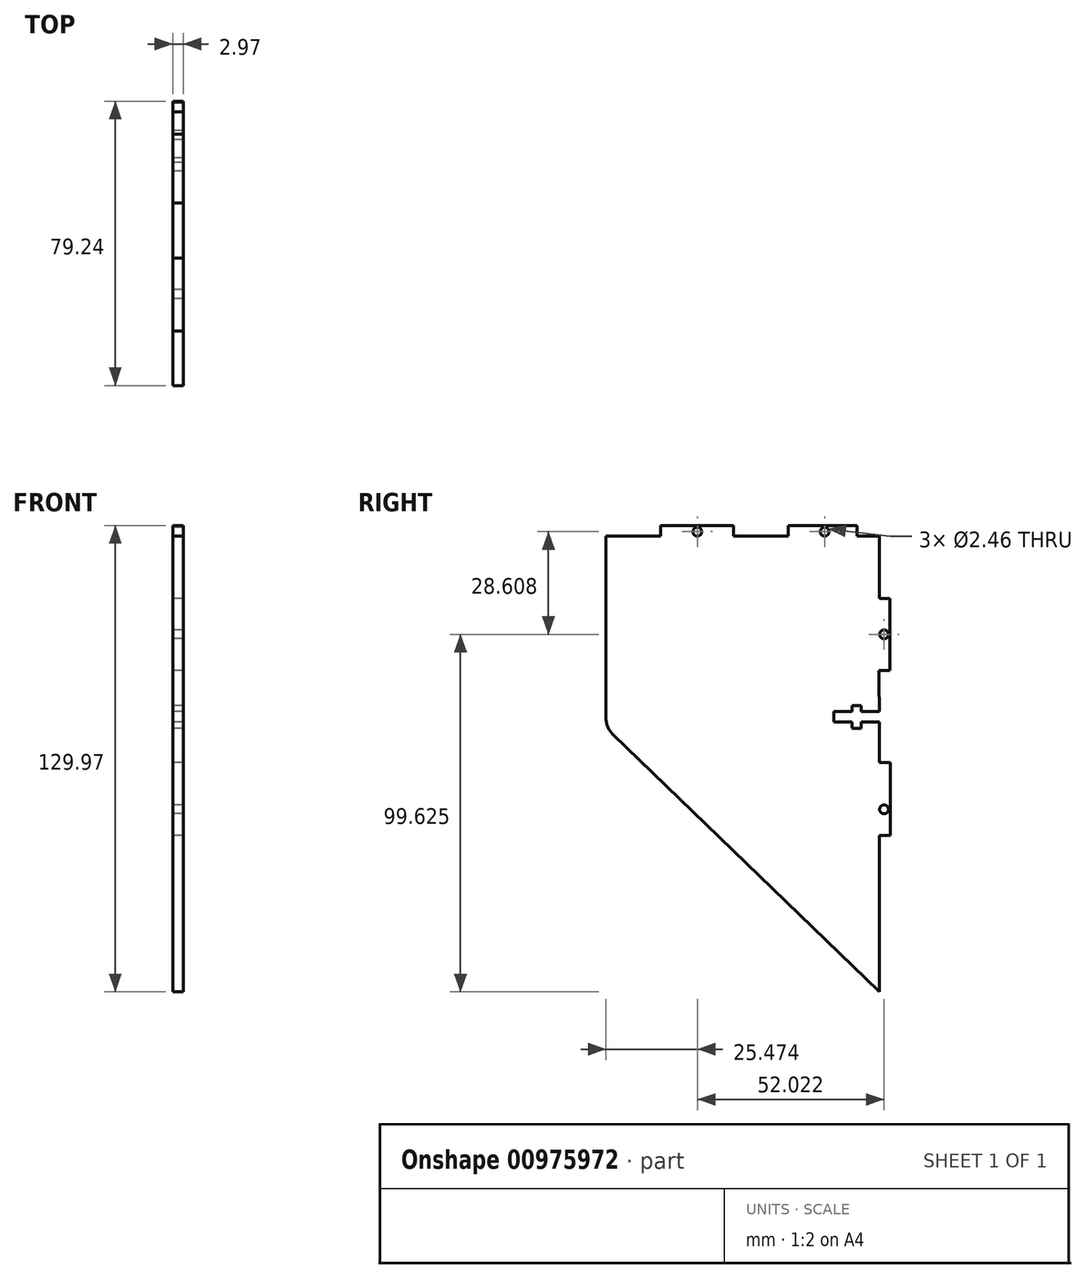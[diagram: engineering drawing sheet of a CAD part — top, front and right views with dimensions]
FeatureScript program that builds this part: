
annotation { "Feature Type Name" : "Feature", "Feature Type Description" : "" }
export const myFeature = defineFeature(function(context is Context, id is Id, definition is map)
    precondition{}
    {
        {
            var Q0;
            Q0=qCreatedBy(makeId("Right.planeOp"),FACE);
            var sketch = newSketch(context, id + "F0", { "sketchPlane" : qUnion([Q0])});
            skLineSegment(sketch, "E0", {"start": v(-31.9, 69.4) * mm, "end": v(-36.98, 69.4) * mm});
            skLineSegment(sketch, "E1", {"start": v(-57.29, 69.4) * mm, "end": v(-72.6, 69.4) * mm});
            skLineSegment(sketch, "E2", {"start": v(-31.9, -16.97) * mm, "end": v(-31.9, -57.6) * mm});
            skLineSegment(sketch, "E3", {"start": v(-92.92, 69.4) * mm, "end": v(-92.92, 72.36) * mm});
            skLineSegment(sketch, "E4", {"start": v(-72.6, 69.4) * mm, "end": v(-72.6, 72.36) * mm});
            skLineSegment(sketch, "E5", {"start": v(-92.92, 72.36) * mm, "end": v(-72.6, 72.36) * mm});
            skLineSegment(sketch, "E6", {"start": v(-108.16, 69.4) * mm, "end": v(-92.92, 69.4) * mm});
            skLineSegment(sketch, "E7", {"start": v(-57.29, 69.4) * mm, "end": v(-57.29, 72.36) * mm});
            skPoint(sketch, "E8", {"position": v(-31.9, 16.05) * mm});
            skPoint(sketch, "E9", {"position": v(-38.33, 19.05) * mm});
            skLineSegment(sketch, "E10.bottom", {"start": v(-39.6, 22.22) * mm, "end": v(-37.06, 22.22) * mm});
            skLineSegment(sketch, "E10.top", {"start": v(-39.6, 15.87) * mm, "end": v(-37.06, 15.87) * mm});
            skLineSegment(sketch, "E11.right", {"start": v(-44.67, 20.51) * mm, "end": v(-44.67, 17.58) * mm});
            skLineSegment(sketch, "E12", {"start": v(-31.99, 20.51) * mm, "end": v(-37.06, 20.51) * mm});
            skLineSegment(sketch, "E13", {"start": v(-39.6, 20.51) * mm, "end": v(-44.67, 20.51) * mm});
            skLineSegment(sketch, "E14", {"start": v(-44.67, 17.58) * mm, "end": v(-39.6, 17.58) * mm});
            skLineSegment(sketch, "E15", {"start": v(-31.99, 17.58) * mm, "end": v(-37.06, 17.58) * mm});
            skLineSegment(sketch, "E16", {"start": v(-39.6, 22.22) * mm, "end": v(-39.6, 20.51) * mm});
            skLineSegment(sketch, "E17", {"start": v(-39.6, 15.87) * mm, "end": v(-39.6, 17.58) * mm});
            skLineSegment(sketch, "E18", {"start": v(-37.06, 22.22) * mm, "end": v(-37.06, 20.51) * mm});
            skLineSegment(sketch, "E19", {"start": v(-37.06, 17.58) * mm, "end": v(-37.06, 15.87) * mm});
            skLineSegment(sketch, "E20", {"start": v(-32.06, 28.75) * mm, "end": v(-31.99, 20.51) * mm});
            skPoint(sketch, "E21", {"position": v(-44.67, 19.05) * mm});
            skLineSegment(sketch, "E22", {"start": v(-106.22, 14.17) * mm, "end": v(-31.9, -57.6) * mm});
            skLineSegment(sketch, "E23", {"start": v(-108.16, 69.4) * mm, "end": v(-108.16, 18.74) * mm});
            skPoint(sketch, "E24", {"position": v(-64.95, 69.4) * mm});
            skCircle(sketch, "E25", {"center": v(-82.69, 70.62) * mm, "radius": 1.23 * mm});
            skPoint(sketch, "E25.first.point", {"position": v(-82.76, 69.4) * mm});
            skPoint(sketch, "E25.third.point", {"position": v(-82.6, 71.85) * mm});
            skPoint(sketch, "E26.MirrorP", {"position": v(-47.28, 71.85) * mm});
            skCircle(sketch, "E27.MirrorC", {"center": v(-47.2, 70.62) * mm, "radius": 1.23 * mm});
            skPoint(sketch, "E28.MirrorP", {"position": v(-47.13, 69.4) * mm});
            skPoint(sketch, "E29.MirrorP", {"position": v(-29.43, -6.7) * mm});
            skPoint(sketch, "E30.MirrorP", {"position": v(-31.9, -6.8) * mm});
            skCircle(sketch, "E31.MirrorC", {"center": v(-30.66, -6.75) * mm, "radius": 1.23 * mm});
            skLineSegment(sketch, "E32", {"start": v(-36.98, 69.4) * mm, "end": v(-38.15, 69.4) * mm});
            skLineSegment(sketch, "E33", {"start": v(-38.15, 69.4) * mm, "end": v(-38.15, 72.36) * mm});
            skLineSegment(sketch, "E34", {"start": v(-57.29, 72.36) * mm, "end": v(-38.15, 72.36) * mm});
            skLineSegment(sketch, "E35", {"start": v(-31.9, 52.07) * mm, "end": v(-29.08, 52.07) * mm});
            skLineSegment(sketch, "E36", {"start": v(-32.06, 31.96) * mm, "end": v(-29.08, 31.96) * mm});
            skLineSegment(sketch, "E37", {"start": v(-32.06, 28.75) * mm, "end": v(-32.06, 31.96) * mm});
            skLineSegment(sketch, "E38", {"start": v(-29.08, 49.07) * mm, "end": v(-29.08, 31.96) * mm});
            skLineSegment(sketch, "E39", {"start": v(-29.08, 49.07) * mm, "end": v(-29.08, 52.07) * mm});
            skLineSegment(sketch, "E40", {"start": v(-31.9, 52.07) * mm, "end": v(-31.9, 69.4) * mm});
            skPoint(sketch, "E41", {"position": v(-31.9, 42.02) * mm});
            skLineSegment(sketch, "E42", {"start": v(-31.9, 42.02) * mm, "end": v(-29.43, 42.02) * mm});
            skCircle(sketch, "E43", {"center": v(-30.66, 42.02) * mm, "radius": 1.23 * mm});
            skLineSegment(sketch, "E44", {"start": v(-31.9, 6.25) * mm, "end": v(-28.92, 6.25) * mm});
            skLineSegment(sketch, "E45", {"start": v(-28.92, 6.25) * mm, "end": v(-28.92, 3.35) * mm});
            skLineSegment(sketch, "E46", {"start": v(-31.9, -16.97) * mm, "end": v(-31.9, -14.04) * mm});
            skLineSegment(sketch, "E47", {"start": v(-31.9, -14.04) * mm, "end": v(-28.92, -14.04) * mm});
            skLineSegment(sketch, "E48", {"start": v(-28.92, -14.04) * mm, "end": v(-28.92, 3.35) * mm});
            skLineSegment(sketch, "E49", {"start": v(-31.99, 17.58) * mm, "end": v(-31.9, 6.25) * mm});
            skPoint(sketch, "E50.visualSharp", {"position": v(-108.16, 16.05) * mm});
            skArc(sketch, "E50.filletArc", {"start": v(-108.16, 18.74) * mm, "mid": v(-107.66, 16.26) * mm, "end": v(-106.22, 14.17) * mm});
            skSolve(sketch);
        }
        {
            var Q0;
            Q0=makeQuery(id+"F0.imprint","IMPRINT",FACE,{"disambiguationData":[TD([[makeQuery(id+"F0.imprint","IMPRINT",EDGE,{"derivedFrom":sQuery(id+"F0.wireOp",EDGE,"SqXUpr0z-BT1b-Fi35-Xfog-EePpgUMi8eG5")}),-1.0]])]});
            var Q1;
            Q1=makeQuery(id+"F0.imprint","IMPRINT",FACE,{"disambiguationData":[TD([[makeQuery(id+"F0.imprint","IMPRINT",EDGE,{"derivedFrom":sQuery(id+"F0.wireOp",EDGE,"E0")}),1.0]])]});
            extrude(context, id + "F1", {"entities" : qUnion([Q0, Q1]), "depth" : 2.97 * mm, "offsetDistance" : 25.4 * mm});
        }
    });
